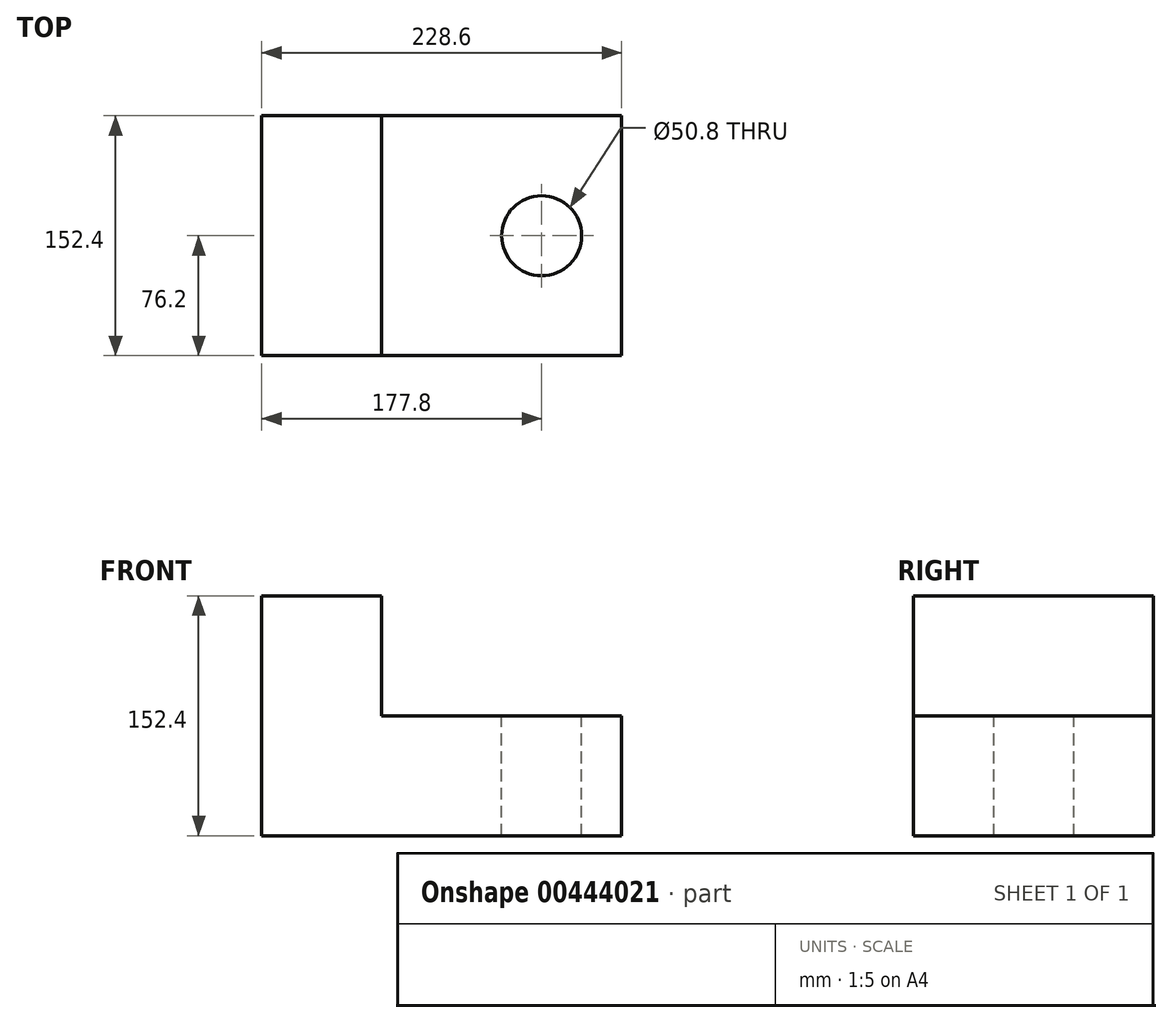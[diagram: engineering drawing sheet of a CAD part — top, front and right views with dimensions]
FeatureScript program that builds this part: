
annotation { "Feature Type Name" : "Feature", "Feature Type Description" : "" }
export const myFeature = defineFeature(function(context is Context, id is Id, definition is map)
    precondition{}
    {
        {
            var Q0;
            Q0=qCreatedBy(makeId("Front.planeOp"),FACE);
            var sketch = newSketch(context, id + "F0", { "sketchPlane" : qUnion([Q0])});
            skLineSegment(sketch, "E0", {"start": v(0, 0) * mm, "end": v(-228.6, 0) * mm});
            skLineSegment(sketch, "E1", {"start": v(-228.6, 0) * mm, "end": v(-228.6, 152.4) * mm});
            skLineSegment(sketch, "E2", {"start": v(-228.6, 152.4) * mm, "end": v(-152.4, 152.4) * mm});
            skLineSegment(sketch, "E3", {"start": v(-152.4, 152.4) * mm, "end": v(-152.4, 76.2) * mm});
            skLineSegment(sketch, "E4", {"start": v(-152.4, 76.2) * mm, "end": v(0, 76.2) * mm});
            skLineSegment(sketch, "E5", {"start": v(0, 76.2) * mm, "end": v(0, 0) * mm});
            skSolve(sketch);
        }
        {
            var Q0;
            Q0=makeQuery(id+"F0.imprint","IMPRINT",FACE,{"disambiguationData":[TD([[makeQuery(id+"F0.imprint","IMPRINT",EDGE,{"derivedFrom":sQuery(id+"F0.wireOp",EDGE,"E0")}),-1.0]])]});
            extrude(context, id + "F1", {"entities" : qUnion([Q0]), "endBound" : BoundingType.SYMMETRIC, "depth" : 152.4 * mm});
        }
        {
            var Q0;
            Q0=makeQuery(id+"F1.opExtrude","SWEPT_FACE",FACE,{"disambiguationData":[OSD([sQuery(id+"F0.wireOp",EDGE,"E4")])]});
            var sketch = newSketch(context, id + "F2", { "sketchPlane" : qUnion([Q0])});
            skPoint(sketch, "E6", {"position": v(-50.8, 0) * mm});
            skSolve(sketch);
        }
        {
            var Q0;
            Q0=sQuery(id+"F2.wireOp",VERTEX,"E6");
            var Q1;
            Q1=makeQuery(id+"F1.opExtrude","SWEPT_BODY",BODY,{"disambiguationData":[OSD([sQuery(id+"F0.wireOp",EDGE,"E0"),sQuery(id+"F0.wireOp",EDGE,"E1"),sQuery(id+"F0.wireOp",EDGE,"E2"),sQuery(id+"F0.wireOp",EDGE,"E3"),sQuery(id+"F0.wireOp",EDGE,"E4"),sQuery(id+"F0.wireOp",EDGE,"E5")])]});
            hole(context, id + "F3", {"style" : HoleStyle.SIMPLE, "endStyle" : HoleEndStyle.THROUGH, "holeDiameter" : 50.8 * mm, "isTappedThrough" : true, "tappedDepth" : 12.7 * mm, "tapClearance" : 3, "locations" : qUnion([Q0]), "scope" : qUnion([Q1])});
        }
    });
